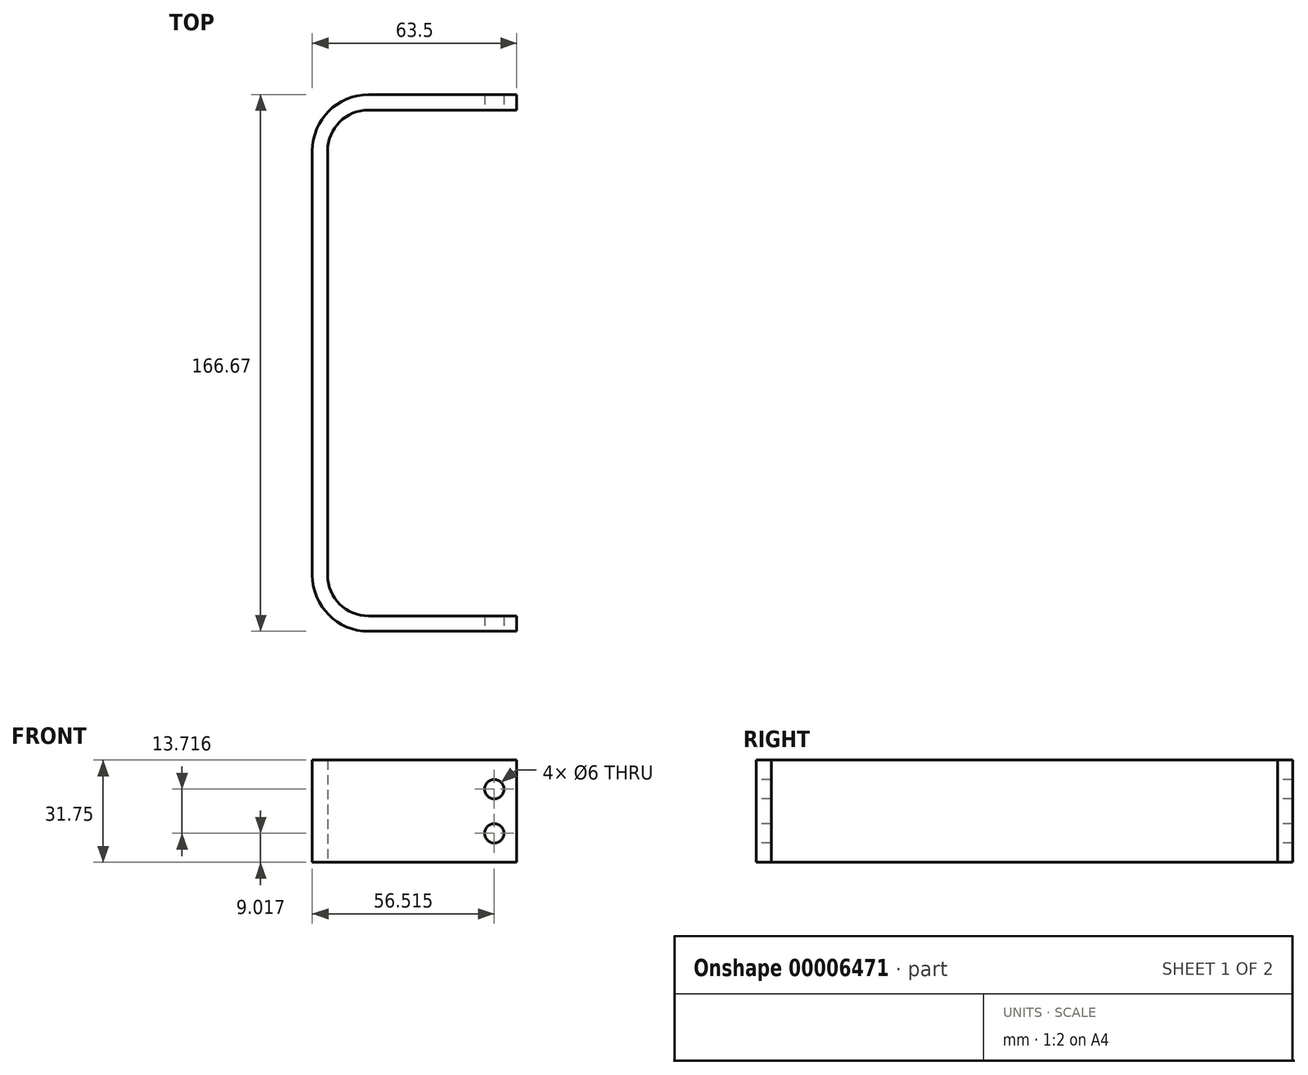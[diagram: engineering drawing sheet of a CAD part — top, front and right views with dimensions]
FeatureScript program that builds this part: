
annotation { "Feature Type Name" : "Feature", "Feature Type Description" : "" }
export const myFeature = defineFeature(function(context is Context, id is Id, definition is map)
    precondition{}
    {
        {
            var Q0;
            Q0=qCreatedBy(makeId("Top.planeOp"),FACE);
            var sketch = newSketch(context, id + "F0", { "sketchPlane" : qUnion([Q0])});
            skLineSegment(sketch, "E0", {"start": v(0, 0) * mm, "end": v(-46.04, 0) * mm});
            skLineSegment(sketch, "E1", {"start": v(-63.5, -17.46) * mm, "end": v(-63.5, -149.21) * mm});
            skLineSegment(sketch, "E2", {"start": v(-46.04, -166.67) * mm, "end": v(0, -166.67) * mm});
            skLineSegment(sketch, "E3", {"start": v(0, -166.67) * mm, "end": v(0, -161.91) * mm});
            skLineSegment(sketch, "E4", {"start": v(0, -161.91) * mm, "end": v(-46.04, -161.91) * mm});
            skLineSegment(sketch, "E5", {"start": v(-58.74, -149.21) * mm, "end": v(-58.74, -17.46) * mm});
            skLineSegment(sketch, "E6", {"start": v(-46.04, -4.76) * mm, "end": v(0, -4.76) * mm});
            skLineSegment(sketch, "E7", {"start": v(0, -4.76) * mm, "end": v(0, 0) * mm});
            skLineSegment(sketch, "E8.bottom", {"start": v(0, -10.15) * mm, "end": v(-26.99, -10.15) * mm, "construction": true});
            skLineSegment(sketch, "E8.top", {"start": v(0, -156.2) * mm, "end": v(-26.99, -156.2) * mm, "construction": true});
            skLineSegment(sketch, "E8.left", {"start": v(0, -10.15) * mm, "end": v(0, -156.2) * mm, "construction": true});
            skLineSegment(sketch, "E8.right", {"start": v(-26.99, -10.15) * mm, "end": v(-26.99, -156.2) * mm, "construction": true});
            skPoint(sketch, "E9.visualSharp", {"position": v(-58.74, -4.76) * mm});
            skArc(sketch, "E9.filletArc", {"start": v(-46.04, -4.76) * mm, "mid": v(-55.02, -8.48) * mm, "end": v(-58.74, -17.46) * mm});
            skPoint(sketch, "E10.visualSharp", {"position": v(-58.74, -161.91) * mm});
            skArc(sketch, "E10.filletArc", {"start": v(-58.74, -149.21) * mm, "mid": v(-55.02, -158.2) * mm, "end": v(-46.04, -161.91) * mm});
            skPoint(sketch, "E11.visualSharp", {"position": v(-63.5, 0) * mm});
            skArc(sketch, "E11.filletArc", {"start": v(-46.04, 0) * mm, "mid": v(-58.39, -5.11) * mm, "end": v(-63.5, -17.46) * mm});
            skPoint(sketch, "E12.visualSharp", {"position": v(-63.5, -166.67) * mm});
            skArc(sketch, "E12.filletArc", {"start": v(-63.5, -149.21) * mm, "mid": v(-58.39, -161.56) * mm, "end": v(-46.04, -166.67) * mm});
            skSolve(sketch);
        }
        {
            var Q0;
            Q0=makeQuery(id+"F0.imprint","IMPRINT",FACE,{"disambiguationData":[TD([[makeQuery(id+"F0.imprint","IMPRINT",EDGE,{"derivedFrom":sQuery(id+"F0.wireOp",EDGE,"E0")}),1.0]])]});
            extrude(context, id + "F1", {"entities" : qUnion([Q0]), "depth" : 31.75 * mm});
        }
        {
            var Q0;
            Q0=makeQuery(id+"F1.opExtrude","SWEPT_FACE",FACE,{"disambiguationData":[OSD([sQuery(id+"F0.wireOp",EDGE,"E2")])]});
            var sketch = newSketch(context, id + "F2", { "sketchPlane" : qUnion([Q0])});
            skCircle(sketch, "E13", {"center": v(-6.98, 22.73) * mm, "radius": 3 * mm});
            skCircle(sketch, "E14", {"center": v(-6.98, 9.02) * mm, "radius": 3 * mm});
            skLineSegment(sketch, "E15", {"start": v(-6.98, 22.73) * mm, "end": v(-6.98, 31.75) * mm, "construction": true});
            skLineSegment(sketch, "E16", {"start": v(-6.99, 9.02) * mm, "end": v(-6.99, 0) * mm, "construction": true});
            skSolve(sketch);
        }
        {
            var Q0;
            Q0 = qSketchRegion(id + "F2", true);
            extrude(context, id + "F3", {"entities" : qUnion([Q0]), "operationType" : NewBodyOperationType.REMOVE, "endBound" : BoundingType.THROUGH_ALL, "oppositeDirection" : true, "depth" : 25.4 * mm});
        }
    });
